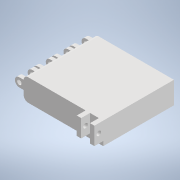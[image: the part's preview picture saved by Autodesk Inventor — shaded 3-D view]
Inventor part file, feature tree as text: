
AUTODESK INVENTOR PART (.ipt)
format: ipt  version: 2022 (Build 260153000, 153)  size: 260,096 bytes
history: native  units: mm
features: extrude x7, sketch x3, other x1, fillet x1
ambient origin geometry x8: Origin, YZ Plane, XZ Plane, XY Plane, X Axis, Y Axis, Z Axis, Center Point
bodies: Solide1 (feature_tree)
feature tree (12):
  extrude  "Extrusion1"  Depth=90.0mm
  extrude  "Extrusion5"  Depth=80.0mm
  extrude  "Extrusion6"  Depth=25.0mm TaperAngle=0.0deg
  extrude  "Extrusion7"  Depth=25.0mm
  other  "Plan de construction3"
  extrude  "Extrusion8"  Depth=20.0mm
  fillet  "Congé3"  Radius=20.0mm
  extrude  "Extrusion9"  Depth=20.0mm
  extrude  "Extrusion10"  Depth=20.0mm
  sketch  "Esquisse13"
  sketch  "Esquisse16"
  sketch  "Esquisse18"
